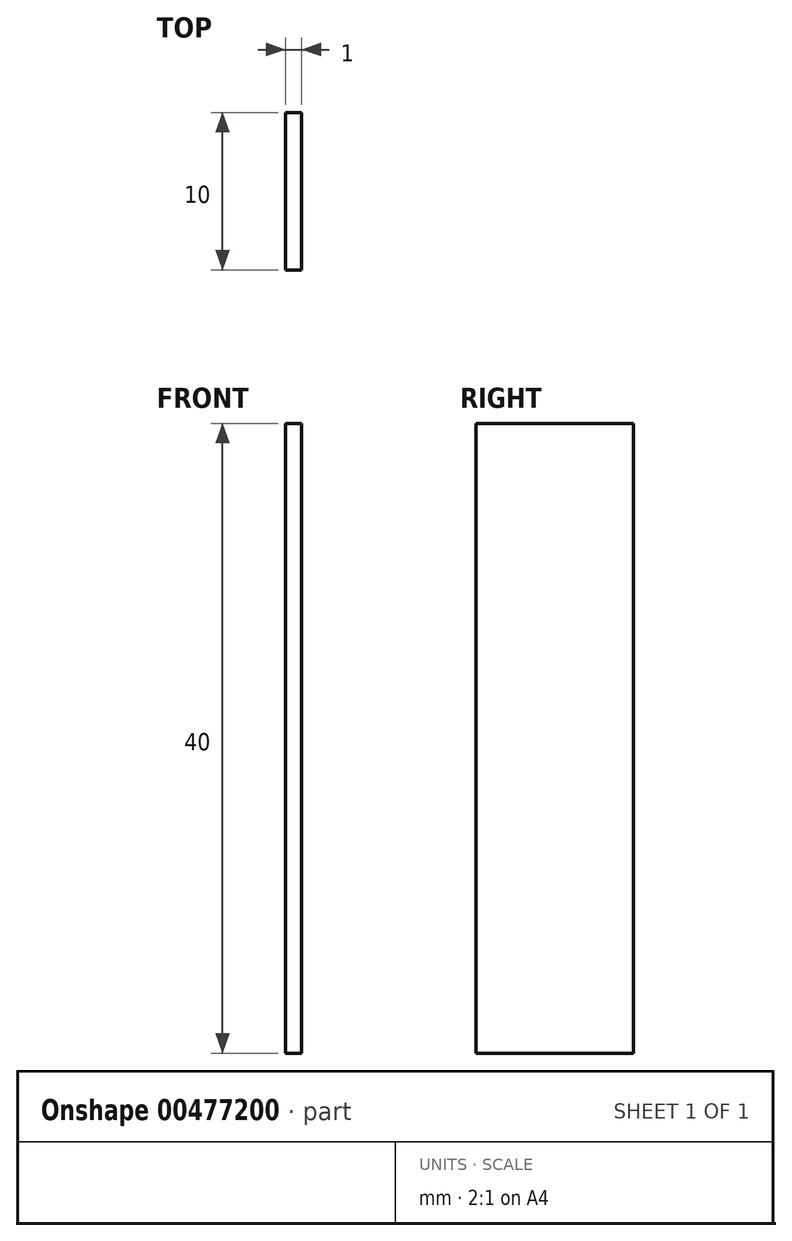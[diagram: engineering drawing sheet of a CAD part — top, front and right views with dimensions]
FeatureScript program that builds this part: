
annotation { "Feature Type Name" : "Feature", "Feature Type Description" : "" }
export const myFeature = defineFeature(function(context is Context, id is Id, definition is map)
    precondition{}
    {
        {
            var Q0;
            Q0=qCreatedBy(makeId("Right.planeOp"),FACE);
            var sketch = newSketch(context, id + "F0", { "sketchPlane" : qUnion([Q0])});
            skLineSegment(sketch, "E0.bottom", {"start": v(-25, -5) * mm, "end": v(-35, -5) * mm});
            skLineSegment(sketch, "E0.top", {"start": v(-25, 35) * mm, "end": v(-35, 35) * mm});
            skLineSegment(sketch, "E0.left", {"start": v(-25, -5) * mm, "end": v(-25, 35) * mm});
            skLineSegment(sketch, "E0.right", {"start": v(-35, -5) * mm, "end": v(-35, 35) * mm});
            skLineSegment(sketch, "E1", {"start": v(-25, -5) * mm, "end": v(-25, 0) * mm});
            skLineSegment(sketch, "E2", {"start": v(-25, 0) * mm, "end": v(0, 0) * mm});
            skLineSegment(sketch, "E3", {"start": v(0, 0) * mm, "end": v(0, 0) * mm});
            skSolve(sketch);
        }
        {
            var Q0;
            Q0=qSketchRegion(id+"F0",true);
            extrude(context, id + "F1", {"entities" : qUnion([Q0]), "endBound" : BoundingType.SYMMETRIC, "depth" : 2 * mm});
        }
        {
            var Q0;
            Q0=qCreatedBy(makeId("Right.planeOp"),FACE);
            var sketch = newSketch(context, id + "F2", { "sketchPlane" : qUnion([Q0])});
            skLineSegment(sketch, "E4.bottom", {"start": v(-49.27, 46.9) * mm, "end": v(-11.45, 46.9) * mm});
            skLineSegment(sketch, "E4.top", {"start": v(-49.27, -14.06) * mm, "end": v(-11.45, -14.06) * mm});
            skLineSegment(sketch, "E4.left", {"start": v(-49.27, 46.9) * mm, "end": v(-49.27, -14.06) * mm});
            skLineSegment(sketch, "E4.right", {"start": v(-11.45, 46.9) * mm, "end": v(-11.45, -14.06) * mm});
            skSolve(sketch);
        }
        {
            var Q0;
            Q0=qSketchRegion(id+"F2",true);
            extrude(context, id + "F3", {"entities" : qUnion([Q0]), "operationType" : NewBodyOperationType.REMOVE, "depth" : 25 * mm});
        }
    });
